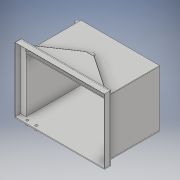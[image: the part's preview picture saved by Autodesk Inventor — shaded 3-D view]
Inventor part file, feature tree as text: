
AUTODESK INVENTOR PART (.ipt)
format: ipt  version: 2019 (Build 230136000, 136)  size: 264,192 bytes
history: native  units: in
note: dims shown in document units (in); Inventor stores cm internally (conversion verified against a paired STEP export)
features: sketch x17, extrude x16, projected_geometry x7
ambient origin geometry x8: Origin, YZ Plane, XZ Plane, XY Plane, X Axis, Y Axis, Z Axis, Center Point
bodies: Solid1 (feature_tree)
feature tree (40):
  extrude  "Extrusion1"  Depth=1.1811in
  extrude  "Extrusion2"  Depth=1.9685in
  extrude  "Extrusion3"  Depth=0.0315in
  extrude  "Extrusion5"  Depth=11.811in TaperAngle=0.0deg
  extrude  "Extrusion7"  Depth=1.1811in TaperAngle=0.0deg
  extrude  "Extrusion10"  Depth=0.0315in TaperAngle=0.0deg
  extrude  "Extrusion12"  Depth=1.1811in
  extrude  "Extrusion13"  Depth=0.0315in
  extrude  "Extrusion14"  Depth=0.0315in TaperAngle=0.0deg
  sketch  "Sketch15"  dims[d46=0.5906in d47=0.0315in d48=0.0in]
  extrude  "Extrusion15"  Depth=0.0315in TaperAngle=0.0deg
  extrude  "Extrusion16"  Depth=0.7874in TaperAngle=0.0deg
  extrude  "Extrusion17"  Depth=0.5906in
  extrude  "Extrusion18"  Depth=1.9685in
  extrude  "Extrusion19"  Depth=0.7874in
  extrude  "Extrusion20"  Depth=0.7874in TaperAngle=0.0deg
  extrude  "Extrusion21"  Depth=0.5906in
  sketch  "Sketch1"  dims[d0=0.3937in d1=1.1811in]
  sketch  "Sketch2"  dims[d2=1.1811in d3=1.9685in]
  projected_geometry  "Projected Loop1"
  sketch  "Sketch3"  dims[d4=0.1969in d5=0.0in d6=0.0315in]
  projected_geometry  "Projected Loop2"
  sketch  "Sketch5"  dims[d7=0.0315in d8=11.811in d9=0.0in]
  projected_geometry  "Projected Loop3"
  sketch  "Sketch7"  dims[d10=0.0315in d11=1.1811in d12=0.0in]
  projected_geometry  "Projected Loop5"
  sketch  "Sketch10"  dims[d17=0.0315in d18=0.0in d22=0.1654in d23=0.0in]
  projected_geometry  "Projected Loop7"
  sketch  "Sketch12"  dims[d29=0.1654in d30=0.0in d35=1.1811in]
  sketch  "Sketch13"  dims[d36=0.0315in d37=0.0in d41=0.0315in]
  sketch  "Sketch14"  dims[d42=0.0315in d43=0.0in d44=0.0315in d45=0.0in]
  projected_geometry  "Projected Loop9"
  sketch  "Sketch16"  dims[d49=0.0394in d50=0.7874in d51=0.0in]
  sketch  "Sketch17"  dims[d52=0.5906in d53=0.5906in]
  sketch  "Sketch18"  dims[d54=1.9685in d55=1.9685in]
  sketch  "Sketch19"  dims[d56=0.7874in d57=0.0in d58=0.0394in]
  sketch  "Sketch20"  dims[d59=0.0394in d60=0.7874in d61=0.0in]
  projected_geometry  "Projected Loop10"
  sketch  "Sketch21"  dims[d62=0.7874in d63=0.0in d64=0.5906in]
  sketch  "Sketch22"  dims[d65=0.7874in d66=0.0in d67=0.0394in d68=0.7874in d69=0.0in]
